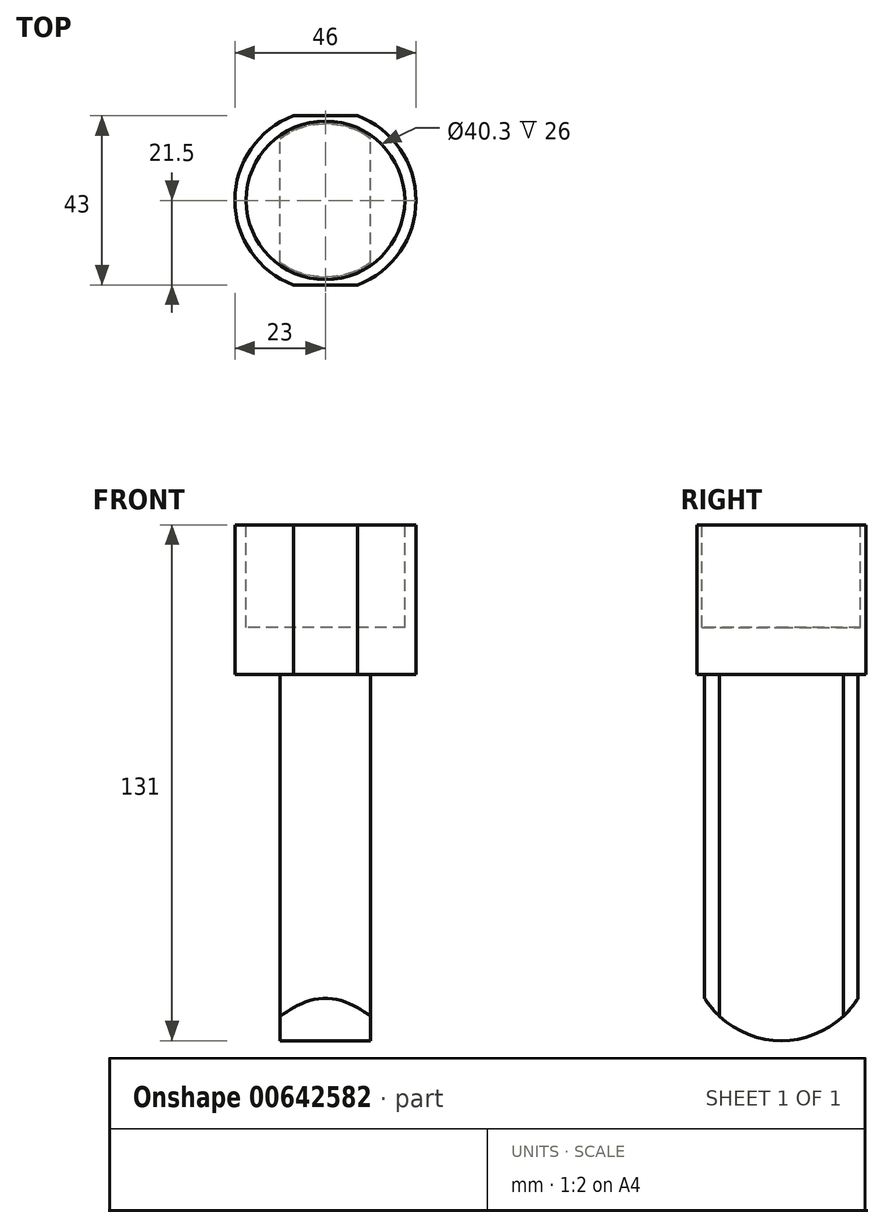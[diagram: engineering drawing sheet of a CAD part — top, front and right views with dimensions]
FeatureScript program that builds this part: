
annotation { "Feature Type Name" : "Feature", "Feature Type Description" : "" }
export const myFeature = defineFeature(function(context is Context, id is Id, definition is map)
    precondition{}
    {
        {
            var Q0;
            Q0=qCreatedBy(makeId("Top.planeOp"),FACE);
            var sketch = newSketch(context, id + "F0", { "sketchPlane" : qUnion([Q0])});
            skArc(sketch, "E0", {"start": v(-8.17, 21.5) * mm, "mid": v(-23, 0) * mm, "end": v(-8.17, -21.5) * mm});
            skLineSegment(sketch, "E1", {"start": v(-8.17, 21.5) * mm, "end": v(8.17, 21.5) * mm});
            skLineSegment(sketch, "E2.MirrorCS", {"start": v(-8.17, -21.5) * mm, "end": v(8.17, -21.5) * mm});
            skArc(sketch, "E3.trimOffspring", {"start": v(8.17, -21.5) * mm, "mid": v(23, 0) * mm, "end": v(8.17, 21.5) * mm});
            skSolve(sketch);
        }
        {
            var Q0;
            Q0 = qSketchRegion(id + "F0", true);
            extrude(context, id + "F1", {"entities" : qUnion([Q0]), "depth" : 38 * mm, "offsetDistance" : 25 * mm});
        }
        {
            var Q0;
            Q0=makeQuery(id+"F1.opExtrude","CAP_FACE",FACE,{"disambiguationData":[OSD([sQuery(id+"F0.wireOp",EDGE,"E0"),sQuery(id+"F0.wireOp",EDGE,"E1"),sQuery(id+"F0.wireOp",EDGE,"E2.MirrorCS"),sQuery(id+"F0.wireOp",EDGE,"E3.trimOffspring")])],"isStart":false});
            var sketch = newSketch(context, id + "F2", { "sketchPlane" : qUnion([Q0])});
            skCircle(sketch, "E4", {"center": v(0, 0) * mm, "radius": 20.15 * mm});
            skSolve(sketch);
        }
        {
            var Q0;
            Q0=makeQuery(id+"F2.imprint","IMPRINT",FACE,{"disambiguationData":[TD([[makeQuery(id+"F2.imprint","IMPRINT",EDGE,{"derivedFrom":sQuery(id+"F2.wireOp",EDGE,"E4")}),1.0]])]});
            var Q1;
            Q1=sQuery(id+"F2.wireOp",EDGE,"E4");
            extrude(context, id + "F3", {"entities" : qUnion([Q0]), "operationType" : NewBodyOperationType.REMOVE, "surfaceEntities" : qUnion([Q1]), "oppositeDirection" : true, "depth" : 26 * mm, "offsetDistance" : 25 * mm});
        }
        {
            var Q0;
            Q0=makeQuery(id+"F1.opExtrude","CAP_FACE",FACE,{"disambiguationData":[OSD([sQuery(id+"F0.wireOp",EDGE,"E0"),sQuery(id+"F0.wireOp",EDGE,"E1"),sQuery(id+"F0.wireOp",EDGE,"E2.MirrorCS"),sQuery(id+"F0.wireOp",EDGE,"E3.trimOffspring")])],"isStart":true});
            var sketch = newSketch(context, id + "F4", { "sketchPlane" : qUnion([Q0])});
            skArc(sketch, "E5", {"start": v(-11.5, -15.75) * mm, "mid": v(0, -19.5) * mm, "end": v(11.5, -15.75) * mm});
            skLineSegment(sketch, "E6", {"start": v(-11.5, 15.75) * mm, "end": v(-11.5, -15.75) * mm});
            skLineSegment(sketch, "E7.MirrorCS", {"start": v(11.5, 15.75) * mm, "end": v(11.5, -15.75) * mm});
            skArc(sketch, "E8.trimOffspring", {"start": v(11.5, 15.75) * mm, "mid": v(0, 19.5) * mm, "end": v(-11.5, 15.75) * mm});
            skSolve(sketch);
        }
        {
            var Q0;
            Q0=makeQuery(id+"F4.imprint","IMPRINT",FACE,{"disambiguationData":[TD([[makeQuery(id+"F4.imprint","IMPRINT",EDGE,{"derivedFrom":sQuery(id+"F4.wireOp",EDGE,"E5")}),1.0]])]});
            extrude(context, id + "F5", {"entities" : qUnion([Q0]), "operationType" : NewBodyOperationType.ADD, "depth" : 93 * mm, "offsetDistance" : 25 * mm});
        }
        {
            var Q0;
            Q0=makeQuery(id+"F5.opExtrude","SWEPT_FACE",FACE,{"disambiguationData":[OSD([sQuery(id+"F4.wireOp",EDGE,"E7.MirrorCS")])]});
            var sketch = newSketch(context, id + "F6", { "sketchPlane" : qUnion([Q0])});
            skArc(sketch, "E9", {"start": v(-21.62, -62.14) * mm, "mid": v(0.74, -92.99) * mm, "end": v(21.07, -60.77) * mm});
            skLineSegment(sketch, "E10", {"start": v(-29.77, -84.58) * mm, "end": v(-29.77, -119.44) * mm});
            skLineSegment(sketch, "E11", {"start": v(-29.77, -119.44) * mm, "end": v(50.88, -114) * mm});
            skLineSegment(sketch, "E12", {"start": v(50.88, -114) * mm, "end": v(28.37, -73.65) * mm});
            skLineSegment(sketch, "E13", {"start": v(28.37, -73.65) * mm, "end": v(21.07, -60.77) * mm});
            skLineSegment(sketch, "E14", {"start": v(-21.62, -62.14) * mm, "end": v(-29.77, -84.58) * mm});
            skSolve(sketch);
        }
        {
            var Q0;
            Q0=makeQuery(id+"F6.imprint","IMPRINT",FACE,{"disambiguationData":[TD([[makeQuery(id+"F6.imprint","IMPRINT",EDGE,{"derivedFrom":sQuery(id+"F6.wireOp",EDGE,"E10")}),1.0]])]});
            var Q1;
            {var subQ0=sQuery(id+"F6.wireOp",EDGE,"E9");var subQ1=sQuery(id+"F4.wireOp",EDGE,"E7.MirrorCS");var subQ4=makeQuery(id+"F5.opExtrude","CAP_EDGE",EDGE,{"disambiguationData":[OSD([subQ1])],"isStart":false});var subQ5=makeQuery(id+"F6.imprint","INTERSECT",VERTEX,{"derivedFrom":[subQ4,subQ0]});Q1=makeQuery(id+"F6.imprint","IMPRINT",FACE,{"disambiguationData":[TD([[makeQuery(id+"F6.imprint","IMPRINT",EDGE,{"disambiguationData":[TD([[subQ5,-1.0]])],"derivedFrom":subQ0}),-1.0]])]});}
            var Q2;
            {var subQ0=sQuery(id+"F6.wireOp",EDGE,"E9");var subQ1=sQuery(id+"F4.wireOp",EDGE,"E7.MirrorCS");var subQ4=makeQuery(id+"F5.opExtrude","CAP_EDGE",EDGE,{"disambiguationData":[OSD([subQ1])],"isStart":false});var subQ5=makeQuery(id+"F6.imprint","INTERSECT",VERTEX,{"derivedFrom":[subQ4,subQ0]});Q2=makeQuery(id+"F6.imprint","IMPRINT",FACE,{"disambiguationData":[TD([[makeQuery(id+"F6.imprint","IMPRINT",EDGE,{"disambiguationData":[TD([[subQ5,1.0]])],"derivedFrom":subQ0}),-1.0]])]});}
            var Q3;
            Q3=sQuery(id+"F6.wireOp",EDGE,"E9");
            var Q4;
            Q4=sQuery(id+"F6.wireOp",EDGE,"E14");
            var Q5;
            Q5=sQuery(id+"F6.wireOp",EDGE,"E10");
            var Q6;
            Q6=sQuery(id+"F6.wireOp",EDGE,"E11");
            var Q7;
            Q7=sQuery(id+"F6.wireOp",EDGE,"E12");
            var Q8;
            Q8=sQuery(id+"F6.wireOp",EDGE,"E13");
            extrude(context, id + "F7", {"entities" : qUnion([Q0, Q1, Q2]), "operationType" : NewBodyOperationType.REMOVE, "surfaceEntities" : qUnion([Q3, Q4, Q5, Q6, Q7, Q8]), "endBound" : BoundingType.THROUGH_ALL, "oppositeDirection" : true, "depth" : 25 * mm, "offsetDistance" : 25 * mm});
        }
    });
